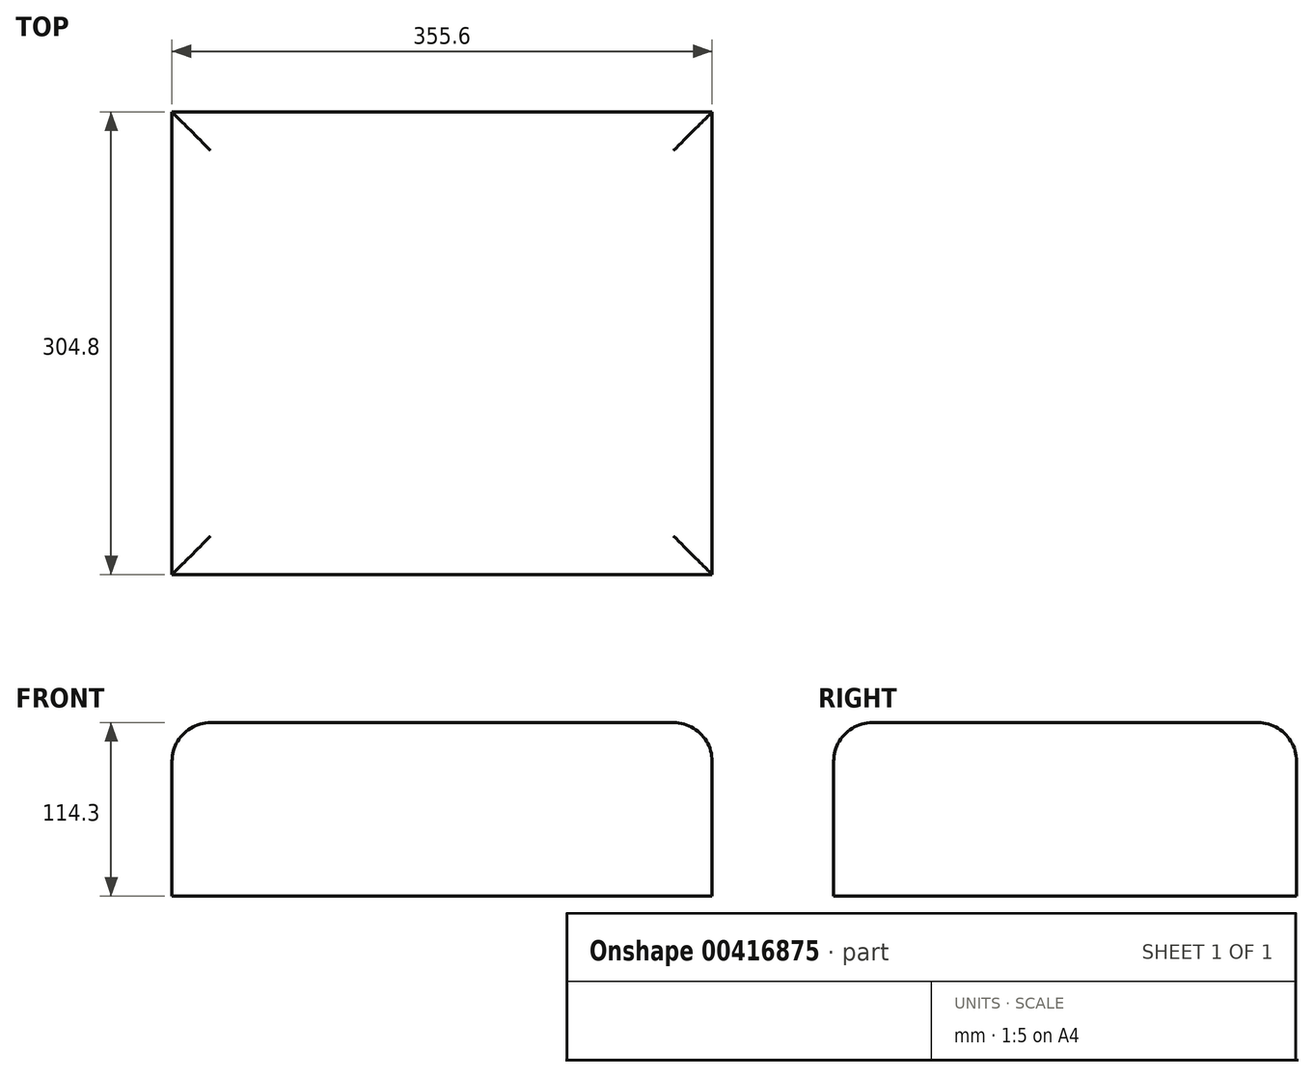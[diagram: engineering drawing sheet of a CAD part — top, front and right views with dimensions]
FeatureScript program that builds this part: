
annotation { "Feature Type Name" : "Feature", "Feature Type Description" : "" }
export const myFeature = defineFeature(function(context is Context, id is Id, definition is map)
    precondition{}
    {
        {
            var Q0;
            Q0=qCreatedBy(makeId("Top.planeOp"),FACE);
            var sketch = newSketch(context, id + "F0", { "sketchPlane" : qUnion([Q0])});
            skLineSegment(sketch, "E0.bottom", {"start": v(-177.8, 152.4) * mm, "end": v(177.8, 152.4) * mm});
            skLineSegment(sketch, "E0.top", {"start": v(-177.8, -152.4) * mm, "end": v(177.8, -152.4) * mm});
            skLineSegment(sketch, "E0.left", {"start": v(-177.8, 152.4) * mm, "end": v(-177.8, -152.4) * mm});
            skLineSegment(sketch, "E0.right", {"start": v(177.8, 152.4) * mm, "end": v(177.8, -152.4) * mm});
            skPoint(sketch, "E0.middle", {"position": v(0, 0) * mm});
            skSolve(sketch);
        }
        {
            var Q0;
            Q0=qSketchRegion(id+"F0",true);
            extrude(context, id + "F1", {"entities" : qUnion([Q0]), "depth" : 25.4 * mm});
        }
        {
            var Q0;
            Q0=makeQuery(id+"F1.opExtrude","CAP_FACE",FACE,{"disambiguationData":[OSD([sQuery(id+"F0.wireOp",EDGE,"E0.bottom"),sQuery(id+"F0.wireOp",EDGE,"E0.top"),sQuery(id+"F0.wireOp",EDGE,"E0.left"),sQuery(id+"F0.wireOp",EDGE,"E0.right")])],"isStart":false});
            var sketch = newSketch(context, id + "F2", { "sketchPlane" : qUnion([Q0])});
            skLineSegment(sketch, "E1.bottom", {"start": v(-177.8, 152.4) * mm, "end": v(177.8, 152.4) * mm});
            skLineSegment(sketch, "E1.top", {"start": v(-177.8, -152.4) * mm, "end": v(177.8, -152.4) * mm});
            skLineSegment(sketch, "E1.left", {"start": v(-177.8, 152.4) * mm, "end": v(-177.8, -152.4) * mm});
            skLineSegment(sketch, "E1.right", {"start": v(177.8, 152.4) * mm, "end": v(177.8, -152.4) * mm});
            skPoint(sketch, "E1.middle", {"position": v(0, 0) * mm});
            skSolve(sketch);
        }
        {
            var Q0;
            Q0=qSketchRegion(id+"F2",true);
            extrude(context, id + "F3", {"entities" : qUnion([Q0]), "operationType" : NewBodyOperationType.ADD, "depth" : 88.9 * mm});
        }
        {
            var Q0;
            Q0=makeQuery(id+"F3.opExtrude","CAP_EDGE",EDGE,{"disambiguationData":[OSD([sQuery(id+"F2.wireOp",EDGE,"E1.left")])],"isStart":false});
            var Q1;
            Q1=makeQuery(id+"F3.opExtrude","CAP_EDGE",EDGE,{"disambiguationData":[OSD([sQuery(id+"F2.wireOp",EDGE,"E1.top")])],"isStart":false});
            var Q2;
            Q2=makeQuery(id+"F3.opExtrude","CAP_EDGE",EDGE,{"disambiguationData":[OSD([sQuery(id+"F2.wireOp",EDGE,"E1.right")])],"isStart":false});
            var Q3;
            Q3=makeQuery(id+"F3.opExtrude","CAP_EDGE",EDGE,{"disambiguationData":[OSD([sQuery(id+"F2.wireOp",EDGE,"E1.bottom")])],"isStart":false});
            fillet(context, id + "F4", {"entities" : qUnion([Q0, Q1, Q2, Q3]), "radius" : 25.4 * mm, "tangentPropagation" : true, "allowEdgeOverflow" : false});
        }
    });
